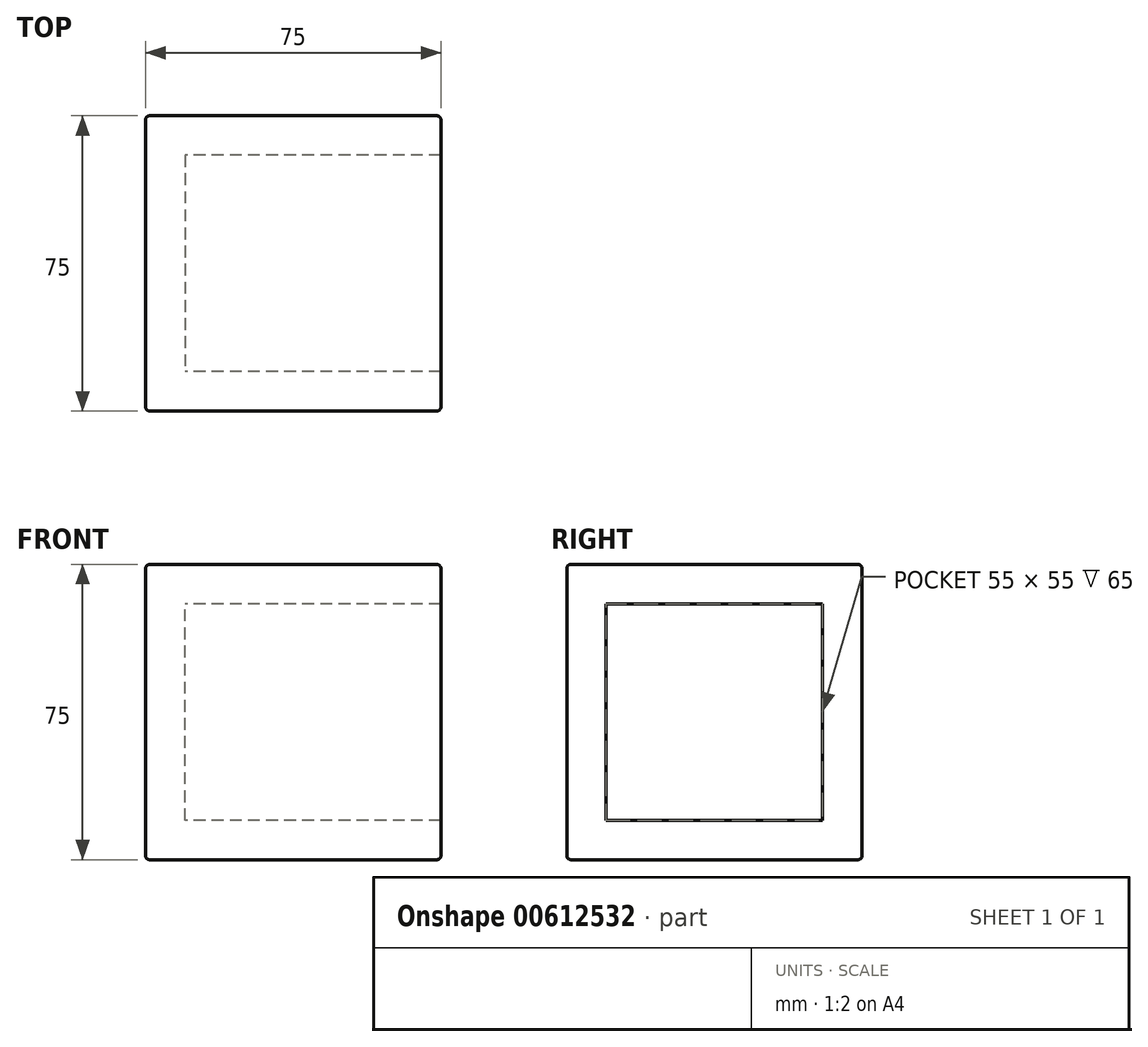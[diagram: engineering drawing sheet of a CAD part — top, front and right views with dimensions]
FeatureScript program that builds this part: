
annotation { "Feature Type Name" : "Feature", "Feature Type Description" : "" }
export const myFeature = defineFeature(function(context is Context, id is Id, definition is map)
    precondition{}
    {
        {
            var Q0;
            Q0=qCreatedBy(makeId("Right.planeOp"),FACE);
            var sketch = newSketch(context, id + "F0", { "sketchPlane" : qUnion([Q0])});
            skLineSegment(sketch, "E0.bottom", {"start": v(26.04, 29.99) * mm, "end": v(-48.96, 29.99) * mm});
            skLineSegment(sketch, "E0.top", {"start": v(26.04, -45.01) * mm, "end": v(-48.96, -45.01) * mm});
            skLineSegment(sketch, "E0.left", {"start": v(26.04, 29.99) * mm, "end": v(26.04, -45.01) * mm});
            skLineSegment(sketch, "E0.right", {"start": v(-48.96, 29.99) * mm, "end": v(-48.96, -45.01) * mm});
            skSolve(sketch);
        }
        {
            var Q0;
            Q0 = qSketchRegion(id + "F0", true);
            extrude(context, id + "F1", {"entities" : qUnion([Q0]), "depth" : 37.5 * mm, "offsetDistance" : 25 * mm});
        }
        {
            var Q0;
            Q0=makeQuery(id+"F1.opExtrude","SWEPT_BODY",BODY,{"disambiguationData":[OSD([sQuery(id+"F0.wireOp",EDGE,"E0.bottom"),sQuery(id+"F0.wireOp",EDGE,"E0.top"),sQuery(id+"F0.wireOp",EDGE,"E0.left"),sQuery(id+"F0.wireOp",EDGE,"E0.right")])]});
            var Q1;
            Q1=qCreatedBy(makeId("Right.planeOp"),FACE);
            mirror(context, id + "F2", {"operationType" : NewBodyOperationType.ADD, "entities" : qUnion([Q0]), "mirrorPlane" : qUnion([Q1])});
        }
        {
            var Q0;
            {var subQ0=makeQuery(id+"F1.opExtrude","SWEPT_EDGE",EDGE,{"disambiguationData":[OSD([sQuery(id+"F0.wireOp",EDGE,"E0.bottom"),sQuery(id+"F0.wireOp",EDGE,"E0.left")])]});Q0=makeQuery(id+"F2.boolean.opBoolean","MERGE",EDGE,{"derivedFrom":[subQ0,makeQuery(id+"F2.opPattern","COPY",EDGE,{"derivedFrom":subQ0,"instanceName":"1"})]});}
            fillet(context, id + "F3", {"entities" : qUnion([Q0]), "radius" : 1 * mm, "tangentPropagation" : true, "allowEdgeOverflow" : false});
        }
        {
            var Q0;
            {var subQ0=makeQuery(id+"F1.opExtrude","SWEPT_EDGE",EDGE,{"disambiguationData":[OSD([sQuery(id+"F0.wireOp",EDGE,"E0.top"),sQuery(id+"F0.wireOp",EDGE,"E0.left")])]});Q0=makeQuery(id+"F2.boolean.opBoolean","MERGE",EDGE,{"derivedFrom":[subQ0,makeQuery(id+"F2.opPattern","COPY",EDGE,{"derivedFrom":subQ0,"instanceName":"1"})]});}
            fillet(context, id + "F4", {"entities" : qUnion([Q0]), "radius" : 1 * mm, "tangentPropagation" : true, "allowEdgeOverflow" : false});
        }
        {
            var Q0;
            Q0=makeQuery(id+"F1.opExtrude","CAP_EDGE",EDGE,{"disambiguationData":[OSD([sQuery(id+"F0.wireOp",EDGE,"E0.left")])],"isStart":false});
            fillet(context, id + "F5", {"entities" : qUnion([Q0]), "radius" : 1 * mm, "tangentPropagation" : true, "allowEdgeOverflow" : false});
        }
        {
            var Q0;
            Q0=makeQuery(id+"F2.opPattern","COPY",EDGE,{"derivedFrom":makeQuery(id+"F1.opExtrude","CAP_EDGE",EDGE,{"disambiguationData":[OSD([sQuery(id+"F0.wireOp",EDGE,"E0.left")])],"isStart":false}),"instanceName":"1"});
            fillet(context, id + "F6", {"entities" : qUnion([Q0]), "radius" : 1 * mm, "tangentPropagation" : true, "allowEdgeOverflow" : false});
        }
        {
            var Q0;
            {var subQ0=makeQuery(id+"F1.opExtrude","SWEPT_EDGE",EDGE,{"disambiguationData":[OSD([sQuery(id+"F0.wireOp",EDGE,"E0.top"),sQuery(id+"F0.wireOp",EDGE,"E0.right")])]});Q0=makeQuery(id+"F2.boolean.opBoolean","MERGE",EDGE,{"derivedFrom":[subQ0,makeQuery(id+"F2.opPattern","COPY",EDGE,{"derivedFrom":subQ0,"instanceName":"1"})]});}
            fillet(context, id + "F7", {"entities" : qUnion([Q0]), "radius" : 1 * mm, "tangentPropagation" : true, "allowEdgeOverflow" : false});
        }
        {
            var Q0;
            Q0=makeQuery(id+"F1.opExtrude","CAP_FACE",FACE,{"disambiguationData":[OSD([sQuery(id+"F0.wireOp",EDGE,"E0.bottom"),sQuery(id+"F0.wireOp",EDGE,"E0.top"),sQuery(id+"F0.wireOp",EDGE,"E0.left"),sQuery(id+"F0.wireOp",EDGE,"E0.right")])],"isStart":false});
            shell(context, id + "F8", {"entities" : qUnion([Q0]), "thickness" : 10 * mm});
        }
    });
